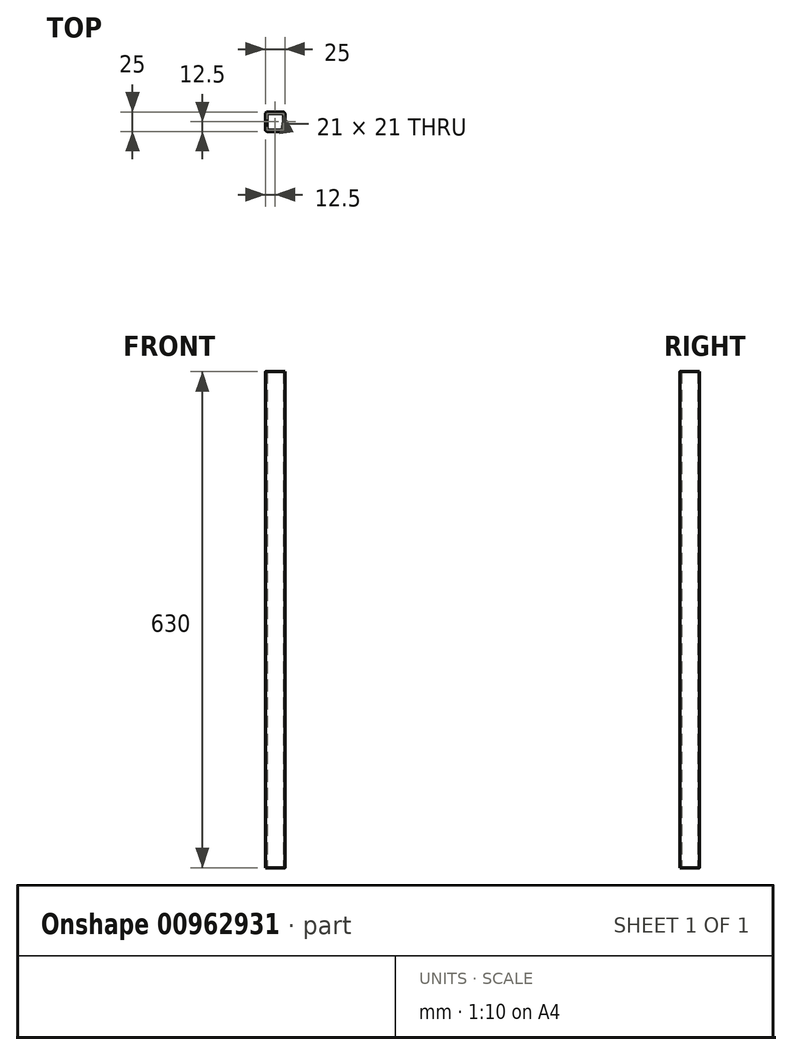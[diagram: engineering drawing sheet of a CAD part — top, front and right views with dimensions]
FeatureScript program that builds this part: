
annotation { "Feature Type Name" : "Feature", "Feature Type Description" : "" }
export const myFeature = defineFeature(function(context is Context, id is Id, definition is map)
    precondition{}
    {
        {
            var Q0;
            Q0=qCreatedBy(makeId("Top.planeOp"),FACE);
            var sketch = newSketch(context, id + "F0", { "sketchPlane" : qUnion([Q0])});
            skLineSegment(sketch, "E0.bottom", {"start": v(9.5, 12.5) * mm, "end": v(-9.5, 12.5) * mm});
            skLineSegment(sketch, "E0.top", {"start": v(9.5, -12.5) * mm, "end": v(-9.5, -12.5) * mm});
            skLineSegment(sketch, "E0.left", {"start": v(12.5, 9.5) * mm, "end": v(12.5, -9.5) * mm});
            skLineSegment(sketch, "E0.right", {"start": v(-12.5, 9.5) * mm, "end": v(-12.5, -9.5) * mm});
            skPoint(sketch, "E0.middle", {"position": v(0, 0) * mm});
            skPoint(sketch, "E1.visualSharp", {"position": v(-12.5, 12.5) * mm});
            skArc(sketch, "E1.filletArc", {"start": v(-9.5, 12.5) * mm, "mid": v(-11.62, 11.62) * mm, "end": v(-12.5, 9.5) * mm});
            skPoint(sketch, "E2.visualSharp", {"position": v(-12.5, -12.5) * mm});
            skArc(sketch, "E2.filletArc", {"start": v(-12.5, -9.5) * mm, "mid": v(-11.62, -11.62) * mm, "end": v(-9.5, -12.5) * mm});
            skPoint(sketch, "E3.visualSharp", {"position": v(12.5, -12.5) * mm});
            skArc(sketch, "E3.filletArc", {"start": v(9.5, -12.5) * mm, "mid": v(11.62, -11.62) * mm, "end": v(12.5, -9.5) * mm});
            skPoint(sketch, "E4.visualSharp", {"position": v(12.5, 12.5) * mm});
            skArc(sketch, "E4.filletArc", {"start": v(12.5, 9.5) * mm, "mid": v(11.62, 11.62) * mm, "end": v(9.5, 12.5) * mm});
            skLineSegment(sketch, "E5.0", {"start": v(10.5, 10.5) * mm, "end": v(-10.5, 10.5) * mm});
            skLineSegment(sketch, "E5.1", {"start": v(10.5, 10.5) * mm, "end": v(10.5, -10.5) * mm});
            skLineSegment(sketch, "E5.2", {"start": v(10.5, -10.5) * mm, "end": v(-10.5, -10.5) * mm});
            skLineSegment(sketch, "E5.3", {"start": v(-10.5, 10.5) * mm, "end": v(-10.5, -10.5) * mm});
            skSolve(sketch);
        }
        {
            var Q0;
            Q0=makeQuery(id+"F0.imprint","IMPRINT",FACE,{"disambiguationData":[TD([[makeQuery(id+"F0.imprint","IMPRINT",EDGE,{"derivedFrom":sQuery(id+"F0.wireOp",EDGE,"E0.bottom")}),1.0]])]});
            extrude(context, id + "F1", {"entities" : qUnion([Q0]), "depth" : 630 * mm, "offsetDistance" : 25 * mm});
        }
    });
